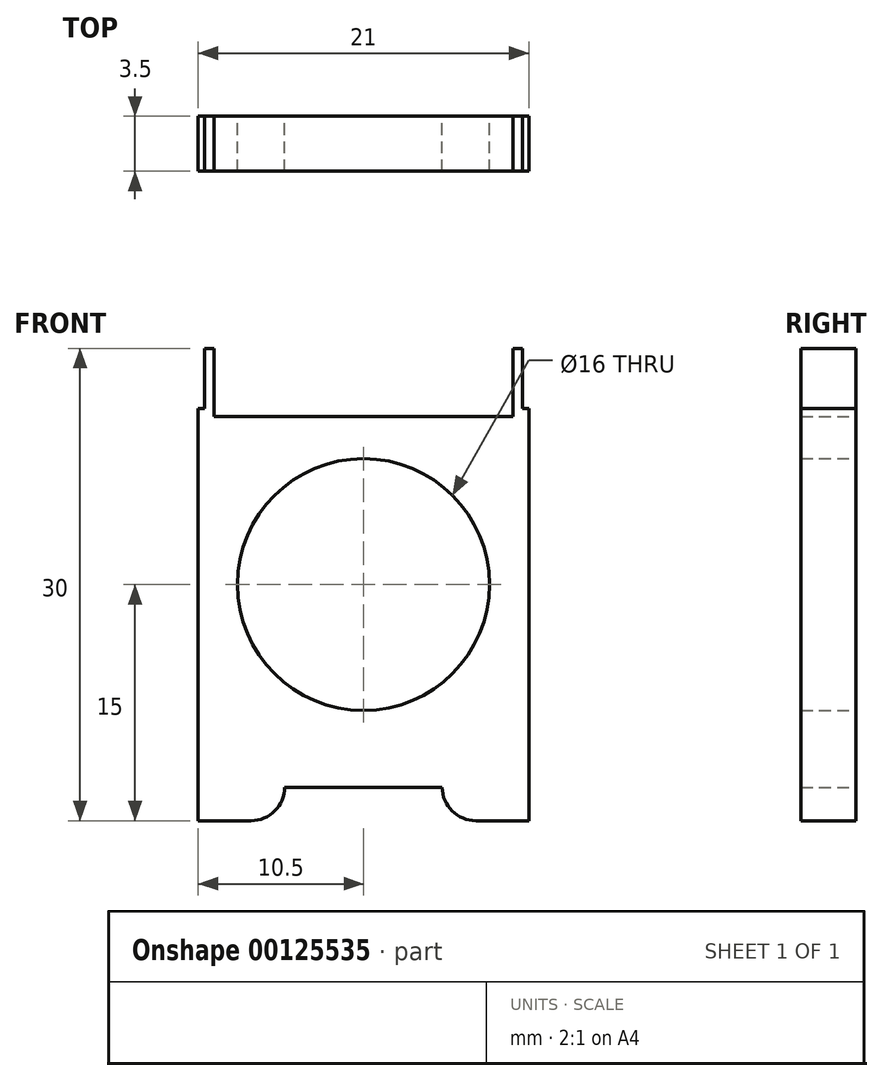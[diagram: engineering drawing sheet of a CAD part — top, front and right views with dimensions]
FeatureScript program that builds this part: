
annotation { "Feature Type Name" : "Feature", "Feature Type Description" : "" }
export const myFeature = defineFeature(function(context is Context, id is Id, definition is map)
    precondition{}
    {
        {
            var Q0;
            Q0=qCreatedBy(makeId("Front.planeOp"),FACE);
            var sketch = newSketch(context, id + "F0", { "sketchPlane" : qUnion([Q0])});
            skLineSegment(sketch, "E0.bottom", {"start": v(10.5, -15) * mm, "end": v(-10.5, -15) * mm});
            skLineSegment(sketch, "E0.top", {"start": v(10.5, 15) * mm, "end": v(-10.5, 15) * mm});
            skLineSegment(sketch, "E0.left", {"start": v(10.5, -15) * mm, "end": v(10.5, 15) * mm});
            skLineSegment(sketch, "E0.right", {"start": v(-10.5, -15) * mm, "end": v(-10.5, 15) * mm});
            skPoint(sketch, "E0.middle", {"position": v(0, 0) * mm});
            skCircle(sketch, "E1", {"center": v(0, 0) * mm, "radius": 8 * mm});
            skLineSegment(sketch, "E2.bottom", {"start": v(5, -15.87) * mm, "end": v(-5, -15.87) * mm});
            skLineSegment(sketch, "E2.top", {"start": v(5, -12.87) * mm, "end": v(-5, -12.87) * mm});
            skLineSegment(sketch, "E2.left", {"start": v(5, -15.87) * mm, "end": v(5, -12.87) * mm});
            skLineSegment(sketch, "E2.right", {"start": v(-5, -15.87) * mm, "end": v(-5, -12.87) * mm});
            skPoint(sketch, "E2.middle", {"position": v(0, -14.37) * mm});
            skLineSegment(sketch, "E3.bottom", {"start": v(-9.5, 15.16) * mm, "end": v(9.5, 15.16) * mm});
            skLineSegment(sketch, "E3.top", {"start": v(-9.5, 10.66) * mm, "end": v(9.5, 10.66) * mm});
            skLineSegment(sketch, "E3.left", {"start": v(-9.5, 15.16) * mm, "end": v(-9.5, 10.66) * mm});
            skLineSegment(sketch, "E3.right", {"start": v(9.5, 15.16) * mm, "end": v(9.5, 10.66) * mm});
            skPoint(sketch, "E3.middle", {"position": v(0, 12.91) * mm});
            skLineSegment(sketch, "E4.bottom", {"start": v(10.5, 11.17) * mm, "end": v(10.1, 11.17) * mm});
            skLineSegment(sketch, "E4.top", {"start": v(10.5, 15.16) * mm, "end": v(10.1, 15.16) * mm});
            skLineSegment(sketch, "E4.left", {"start": v(10.5, 11.17) * mm, "end": v(10.5, 15.16) * mm});
            skLineSegment(sketch, "E4.right", {"start": v(10.1, 11.17) * mm, "end": v(10.1, 15.16) * mm});
            skLineSegment(sketch, "E5.MirrorCS", {"start": v(-10.5, 11.17) * mm, "end": v(-10.1, 11.17) * mm});
            skLineSegment(sketch, "E6.MirrorCS", {"start": v(-10.5, 15.16) * mm, "end": v(-10.1, 15.16) * mm});
            skLineSegment(sketch, "E7.MirrorCS", {"start": v(-10.5, 11.17) * mm, "end": v(-10.5, 15.16) * mm});
            skLineSegment(sketch, "E8.MirrorCS", {"start": v(-10.1, 11.17) * mm, "end": v(-10.1, 15.16) * mm});
            skSolve(sketch);
        }
        {
            var Q0;
            Q0=makeQuery(id+"F0.imprint","IMPRINT",FACE,{"disambiguationData":[TD([[makeQuery(id+"F0.imprint","IMPRINT",EDGE,{"derivedFrom":sQuery(id+"F0.wireOp",EDGE,"E0.top")}),1.0]])]});
            extrude(context, id + "F1", {"entities" : qUnion([Q0]), "depth" : 3.5 * mm});
        }
        {
            var Q0;
            Q0=makeQuery(id+"F1.opExtrude","SWEPT_EDGE",EDGE,{"disambiguationData":[OSD([sQuery(id+"F0.wireOp",EDGE,"E0.bottom"),sQuery(id+"F0.wireOp",EDGE,"E2.right")])]});
            var Q1;
            Q1=makeQuery(id+"F1.opExtrude","SWEPT_EDGE",EDGE,{"disambiguationData":[OSD([sQuery(id+"F0.wireOp",EDGE,"E0.bottom"),sQuery(id+"F0.wireOp",EDGE,"E2.left")])]});
            fillet(context, id + "F2", {"entities" : qUnion([Q0, Q1]), "radius" : 2.14 * mm, "tangentPropagation" : true, "allowEdgeOverflow" : false});
        }
    });
